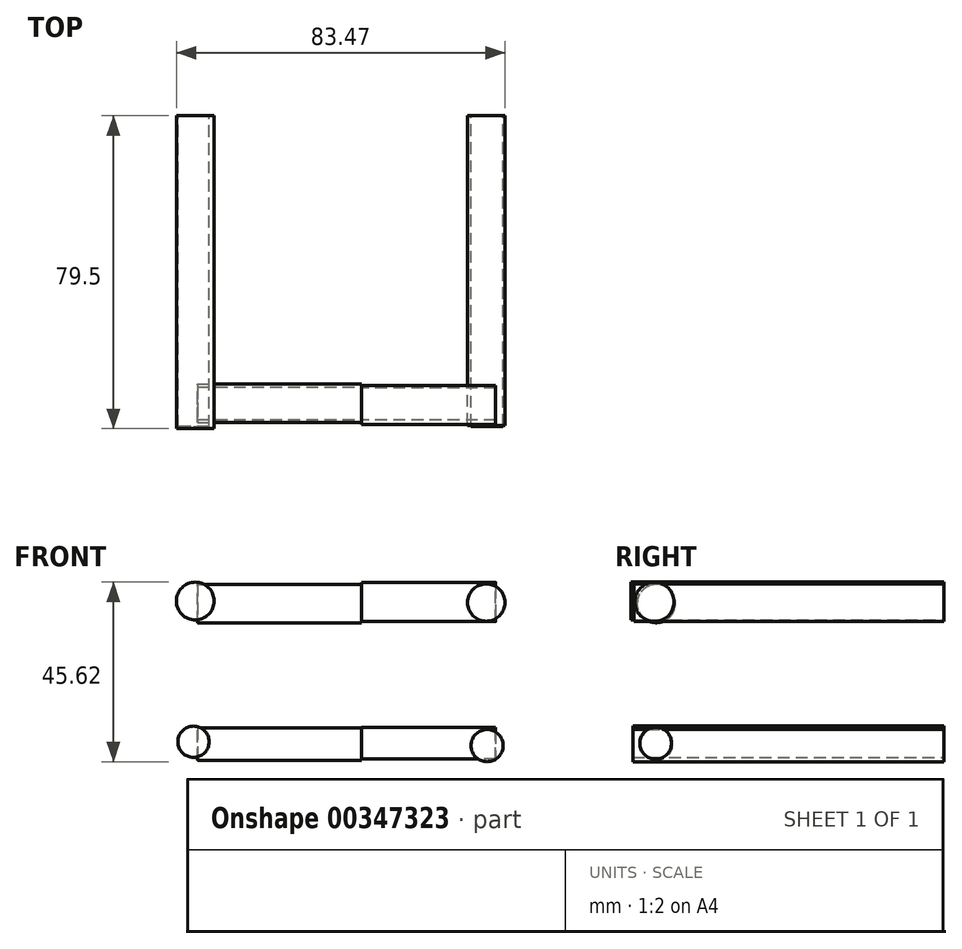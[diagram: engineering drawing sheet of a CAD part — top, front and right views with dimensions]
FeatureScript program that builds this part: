
annotation { "Feature Type Name" : "Feature", "Feature Type Description" : "" }
export const myFeature = defineFeature(function(context is Context, id is Id, definition is map)
    precondition{}
    {
        {
            var Q0;
            Q0=qCreatedBy(makeId("Front.planeOp"),FACE);
            var sketch = newSketch(context, id + "F0", { "sketchPlane" : qUnion([Q0])});
            skCircle(sketch, "E0", {"center": v(-42.3, 40.82) * mm, "radius": 4.8 * mm});
            skSolve(sketch);
        }
        {
            var Q0;
            Q0=makeQuery(id+"F0.imprint","IMPRINT",FACE,{"disambiguationData":[TD([[makeQuery(id+"F0.imprint","IMPRINT",EDGE,{"derivedFrom":sQuery(id+"F0.wireOp",EDGE,"E0")}),1.0]])]});
            extrude(context, id + "F1", {"entities" : qUnion([Q0]), "depth" : 79.5 * mm});
        }
        {
            var Q0;
            Q0=qCreatedBy(makeId("Front.planeOp"),FACE);
            var sketch = newSketch(context, id + "F2", { "sketchPlane" : qUnion([Q0])});
            skCircle(sketch, "E1", {"center": v(31.65, 40.44) * mm, "radius": 4.74 * mm});
            skSolve(sketch);
        }
        {
            var Q0;
            Q0=makeQuery(id+"F2.imprint","IMPRINT",FACE,{"disambiguationData":[TD([[makeQuery(id+"F2.imprint","IMPRINT",EDGE,{"derivedFrom":sQuery(id+"F2.wireOp",EDGE,"E1")}),1.0]])]});
            extrude(context, id + "F3", {"entities" : qUnion([Q0]), "depth" : 78.74 * mm});
        }
        {
            var Q0;
            Q0=qCreatedBy(makeId("Top.planeOp"),FACE);
            var sketch = newSketch(context, id + "F4", { "sketchPlane" : qUnion([Q0])});
            skCircle(sketch, "E2", {"center": v(-42.53, -3.86) * mm, "radius": 4 * mm});
            skCircle(sketch, "E3", {"center": v(31.75, -2.98) * mm, "radius": 4.66 * mm});
            skSolve(sketch);
        }
        {
            var Q0;
            Q0=sQuery(id+"F4.wireOp",EDGE,"E2");
            var Q1;
            Q1=sQuery(id+"F4.wireOp",EDGE,"E3");
            extrude(context, id + "F5", {"bodyType" : ToolBodyType.SURFACE, "surfaceEntities" : qUnion([Q0, Q1]), "depth" : 44.7 * mm});
        }
        {
            var Q0;
            Q0=qCreatedBy(makeId("Front.planeOp"),FACE);
            var sketch = newSketch(context, id + "F6", { "sketchPlane" : qUnion([Q0])});
            skCircle(sketch, "E4", {"center": v(31.85, 4.09) * mm, "radius": 4.09 * mm});
            skCircle(sketch, "E5", {"center": v(-42.75, 5.08) * mm, "radius": 3.97 * mm});
            skSolve(sketch);
        }
        {
            var Q0;
            Q0=makeQuery(id+"F6.imprint","IMPRINT",FACE,{"disambiguationData":[TD([[makeQuery(id+"F6.imprint","IMPRINT",EDGE,{"derivedFrom":sQuery(id+"F6.wireOp",EDGE,"E4")}),1.0]])]});
            var Q1;
            Q1=makeQuery(id+"F6.imprint","IMPRINT",FACE,{"disambiguationData":[TD([[makeQuery(id+"F6.imprint","IMPRINT",EDGE,{"derivedFrom":sQuery(id+"F6.wireOp",EDGE,"E5")}),1.0]])]});
            extrude(context, id + "F7", {"entities" : qUnion([Q0, Q1]), "depth" : 79 * mm});
        }
        {
            var Q0;
            Q0=qCreatedBy(makeId("Right.planeOp"),FACE);
            var sketch = newSketch(context, id + "F8", { "sketchPlane" : qUnion([Q0])});
            skCircle(sketch, "E6", {"center": v(-73.51, 40.62) * mm, "radius": 4.98 * mm});
            skCircle(sketch, "E7", {"center": v(-73.21, 4.7) * mm, "radius": 4.03 * mm});
            skSolve(sketch);
        }
        {
            var Q0;
            Q0 = qSketchRegion(id + "F8", true);
            extrude(context, id + "F9", {"entities" : qUnion([Q0]), "depth" : 34.04 * mm});
        }
        {
            var Q0;
            Q0=qCreatedBy(makeId("Right.planeOp"),FACE);
            var sketch = newSketch(context, id + "F10", { "sketchPlane" : qUnion([Q0])});
            skCircle(sketch, "E8", {"center": v(-73.02, 4.44) * mm, "radius": 4.1 * mm});
            skCircle(sketch, "E9", {"center": v(-73.06, 40.18) * mm, "radius": 4.86 * mm});
            skSolve(sketch);
        }
        {
            var Q0;
            Q0=makeQuery(id+"F10.imprint","IMPRINT",FACE,{"disambiguationData":[TD([[makeQuery(id+"F10.imprint","IMPRINT",EDGE,{"derivedFrom":sQuery(id+"F10.wireOp",EDGE,"E9")}),1.0]])]});
            var Q1;
            Q1=makeQuery(id+"F10.imprint","IMPRINT",FACE,{"disambiguationData":[TD([[makeQuery(id+"F10.imprint","IMPRINT",EDGE,{"derivedFrom":sQuery(id+"F10.wireOp",EDGE,"E8")}),1.0]])]});
            extrude(context, id + "F11", {"entities" : qUnion([Q0, Q1]), "oppositeDirection" : true, "depth" : 41.66 * mm});
        }
    });
